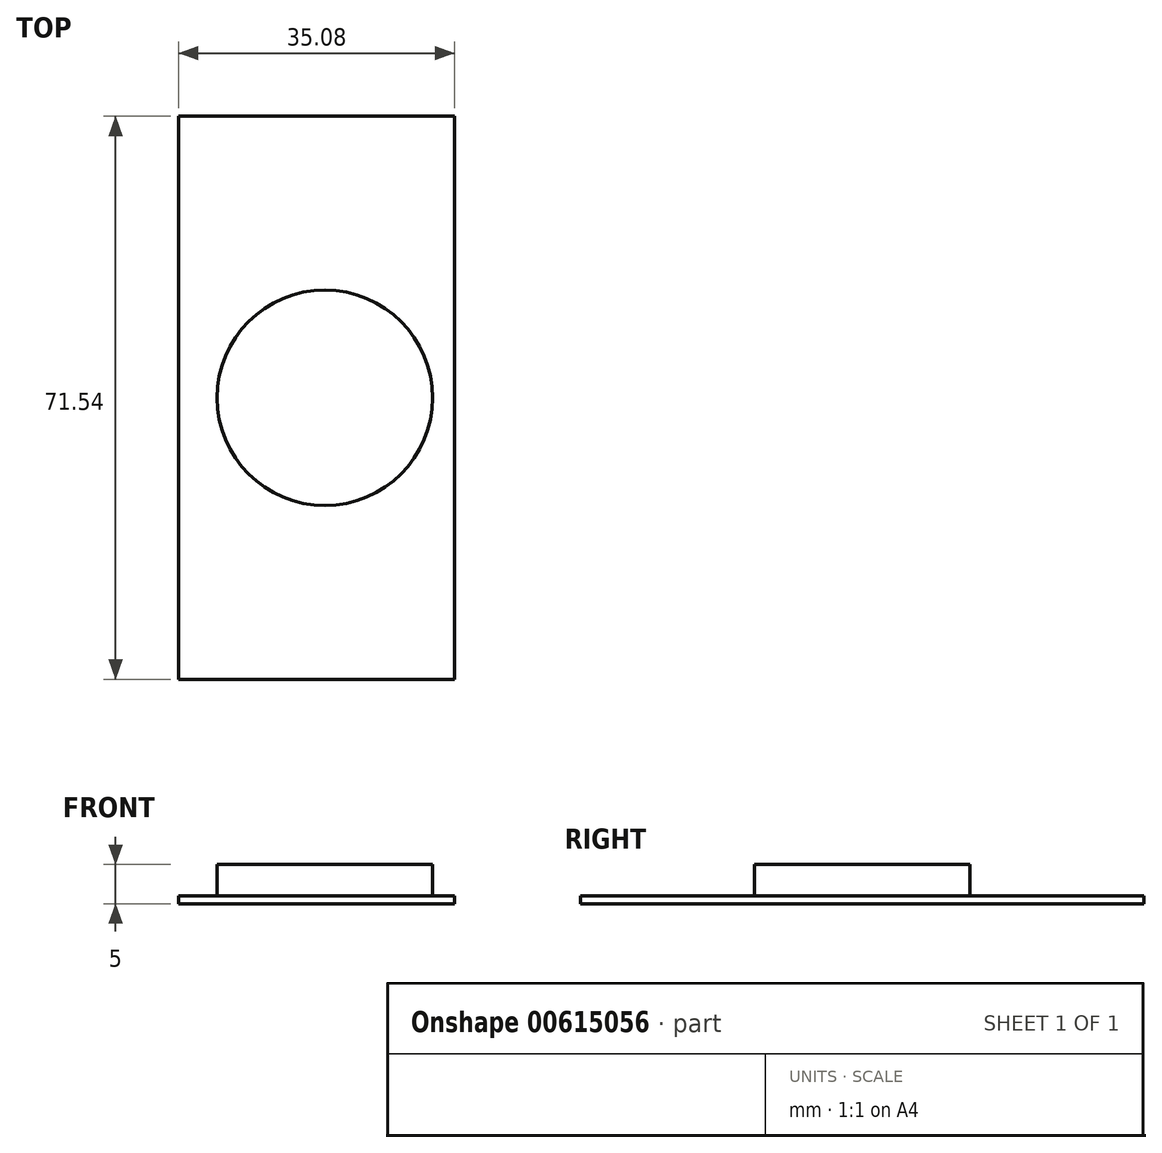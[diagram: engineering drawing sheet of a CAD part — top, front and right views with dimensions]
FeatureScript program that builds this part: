
annotation { "Feature Type Name" : "Feature", "Feature Type Description" : "" }
export const myFeature = defineFeature(function(context is Context, id is Id, definition is map)
    precondition{}
    {
        {
            var Q0;
            Q0=qCreatedBy(makeId("Top.planeOp"),FACE);
            var sketch = newSketch(context, id + "F0", { "sketchPlane" : qUnion([Q0])});
            skLineSegment(sketch, "E0.bottom", {"start": v(278.38, -31.27) * mm, "end": v(-466.68, -31.27) * mm});
            skLineSegment(sketch, "E0.top", {"start": v(278.38, 94.72) * mm, "end": v(-466.68, 94.72) * mm});
            skLineSegment(sketch, "E0.left", {"start": v(278.38, -31.27) * mm, "end": v(278.38, 94.72) * mm});
            skLineSegment(sketch, "E0.right", {"start": v(-466.68, -31.27) * mm, "end": v(-466.68, 94.72) * mm});
            skPoint(sketch, "E0.middle", {"position": v(-94.15, 31.72) * mm});
            skSolve(sketch);
        }
        {
            var Q0;
            Q0=makeQuery(id+"F0.imprint","IMPRINT",FACE,{"disambiguationData":[TD([[makeQuery(id+"F0.imprint","IMPRINT",EDGE,{"derivedFrom":sQuery(id+"F0.wireOp",EDGE,"E0.bottom")}),-1.0]])]});
            var sketch = newSketch(context, id + "F1", { "sketchPlane" : qUnion([Q0])});
            skLineSegment(sketch, "E1.bottom", {"start": v(17.54, 35.77) * mm, "end": v(-17.54, 35.77) * mm});
            skLineSegment(sketch, "E1.top", {"start": v(17.54, -35.77) * mm, "end": v(-17.54, -35.77) * mm});
            skLineSegment(sketch, "E1.left", {"start": v(17.54, 35.77) * mm, "end": v(17.54, -35.77) * mm});
            skLineSegment(sketch, "E1.right", {"start": v(-17.54, 35.77) * mm, "end": v(-17.54, -35.77) * mm});
            skPoint(sketch, "E1.middle", {"position": v(0, 0) * mm});
            skSolve(sketch);
        }
        {
            var Q0;
            Q0 = qSketchRegion(id + "F1", true);
            extrude(context, id + "F2", {"entities" : qUnion([Q0]), "depth" : 1 * mm, "offsetDistance" : 25 * mm});
        }
        {
            var Q0;
            Q0=makeQuery(id+"F2.opExtrude","CAP_FACE",FACE,{"disambiguationData":[OSD([sQuery(id+"F1.wireOp",EDGE,"E1.bottom"),sQuery(id+"F1.wireOp",EDGE,"E1.top"),sQuery(id+"F1.wireOp",EDGE,"E1.left"),sQuery(id+"F1.wireOp",EDGE,"E1.right")])],"isStart":false});
            var sketch = newSketch(context, id + "F3", { "sketchPlane" : qUnion([Q0])});
            skCircle(sketch, "E2", {"center": v(1.05, 0) * mm, "radius": 13.68 * mm});
            skSolve(sketch);
        }
        {
            var Q0;
            Q0 = qSketchRegion(id + "F3", true);
            extrude(context, id + "F4", {"entities" : qUnion([Q0]), "operationType" : NewBodyOperationType.ADD, "depth" : 4 * mm, "offsetDistance" : 25 * mm});
        }
    });
